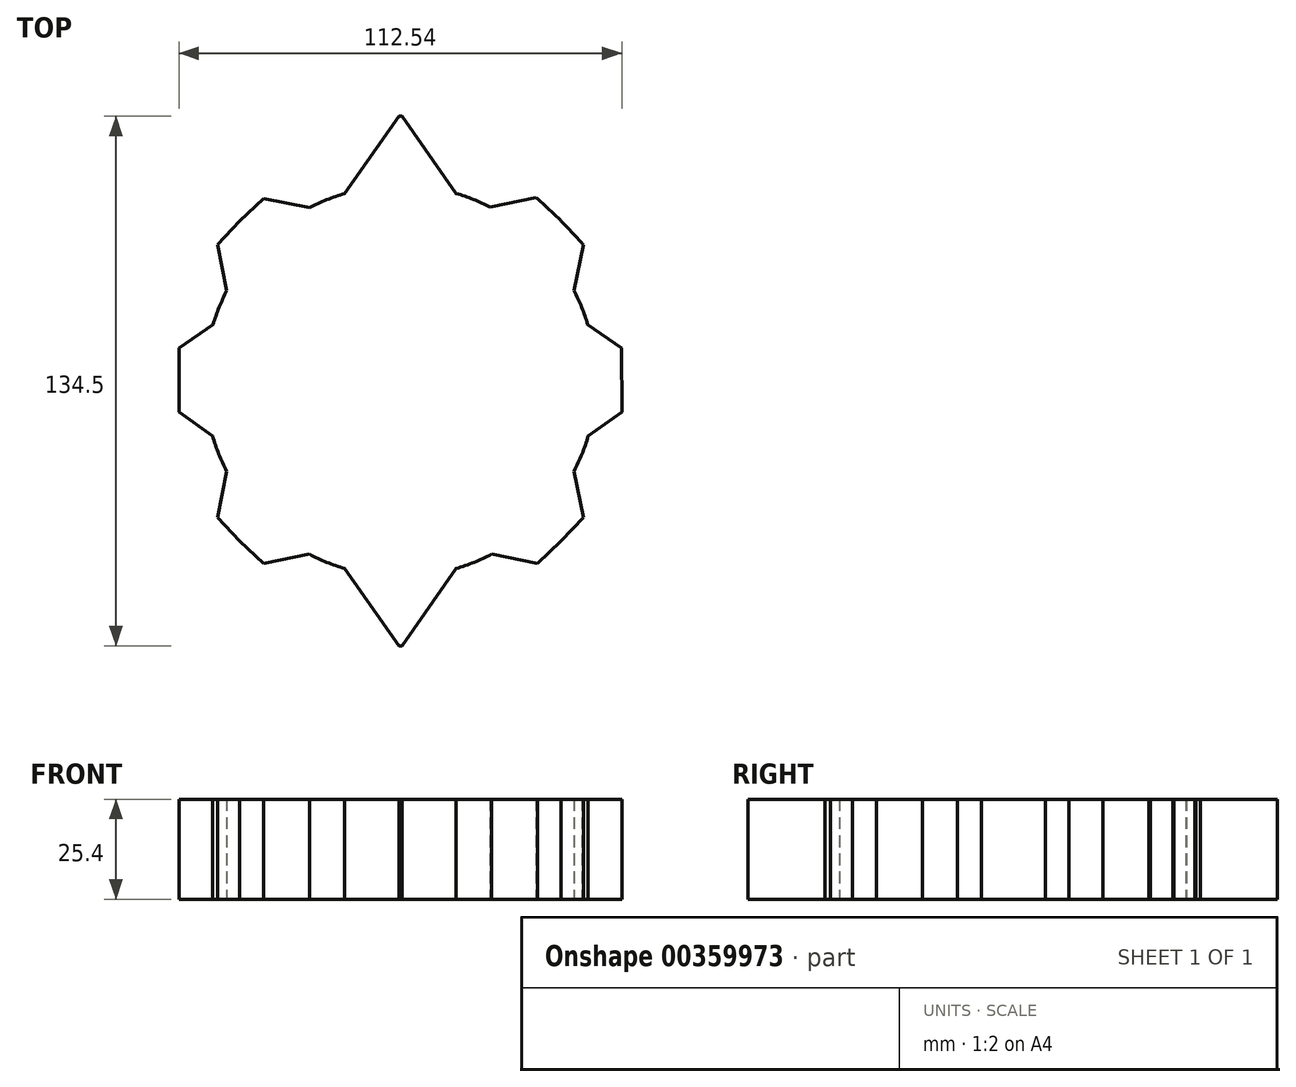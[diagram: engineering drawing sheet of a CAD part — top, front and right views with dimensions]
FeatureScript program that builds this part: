
annotation { "Feature Type Name" : "Feature", "Feature Type Description" : "" }
export const myFeature = defineFeature(function(context is Context, id is Id, definition is map)
    precondition{}
    {
        {
            var Q0;
            Q0=qCreatedBy(makeId("Top.planeOp"),FACE);
            var sketch = newSketch(context, id + "F0", { "sketchPlane" : qUnion([Q0])});
            skCircle(sketch, "E0", {"center": v(0, 0) * mm, "radius": 49.71 * mm});
            skLineSegment(sketch, "E1", {"start": v(0, -67.25) * mm, "end": v(-0.36, -67.25) * mm});
            skLineSegment(sketch, "E2", {"start": v(-0.36, -67.25) * mm, "end": v(-14.16, -47.65) * mm});
            skLineSegment(sketch, "E3.MirrorCS", {"start": v(0.36, -67.25) * mm, "end": v(14.16, -47.65) * mm});
            skLineSegment(sketch, "E4.MirrorCS", {"start": v(0, -67.25) * mm, "end": v(0.36, -67.25) * mm});
            skLineSegment(sketch, "E5.MirrorCS", {"start": v(46.47, -34.62) * mm, "end": v(44.1, -22.94) * mm});
            skLineSegment(sketch, "E6.MirrorCS", {"start": v(40.86, -40.7) * mm, "end": v(46.47, -34.62) * mm});
            skLineSegment(sketch, "E7.MirrorCS", {"start": v(34.82, -46.32) * mm, "end": v(23.13, -44) * mm});
            skLineSegment(sketch, "E8.MirrorCS", {"start": v(40.86, -40.7) * mm, "end": v(34.82, -46.32) * mm});
            skLineSegment(sketch, "E9.MirrorCS", {"start": v(-40.86, -40.7) * mm, "end": v(-34.82, -46.32) * mm});
            skLineSegment(sketch, "E10.MirrorCS", {"start": v(-40.86, -40.7) * mm, "end": v(-46.47, -34.62) * mm});
            skLineSegment(sketch, "E11.MirrorCS", {"start": v(-46.47, -34.62) * mm, "end": v(-44.1, -22.94) * mm});
            skLineSegment(sketch, "E12.MirrorCS", {"start": v(-34.82, -46.32) * mm, "end": v(-23.13, -44) * mm});
            skLineSegment(sketch, "E13.MirrorCS", {"start": v(40.86, 40.7) * mm, "end": v(46.47, 34.62) * mm});
            skLineSegment(sketch, "E14.MirrorCS", {"start": v(40.86, 40.7) * mm, "end": v(34.82, 46.32) * mm});
            skLineSegment(sketch, "E15.MirrorCS", {"start": v(-40.86, 40.7) * mm, "end": v(-46.47, 34.62) * mm});
            skLineSegment(sketch, "E16.MirrorCS", {"start": v(-40.86, 40.7) * mm, "end": v(-34.82, 46.32) * mm});
            skLineSegment(sketch, "E17.MirrorCS", {"start": v(-46.47, 34.62) * mm, "end": v(-44.1, 22.94) * mm});
            skLineSegment(sketch, "E18.MirrorCS", {"start": v(0, 67.25) * mm, "end": v(0.36, 67.25) * mm});
            skLineSegment(sketch, "E19.MirrorCS", {"start": v(-0.36, 67.25) * mm, "end": v(-14.16, 47.65) * mm});
            skLineSegment(sketch, "E20.MirrorCS", {"start": v(-34.82, 46.32) * mm, "end": v(-23.13, 44) * mm});
            skLineSegment(sketch, "E21.MirrorCS", {"start": v(0, 67.25) * mm, "end": v(-0.36, 67.25) * mm});
            skLineSegment(sketch, "E22.MirrorCS", {"start": v(46.47, 34.62) * mm, "end": v(44.1, 22.94) * mm});
            skLineSegment(sketch, "E23.MirrorCS", {"start": v(0.36, 67.25) * mm, "end": v(14.16, 47.65) * mm});
            skLineSegment(sketch, "E24.MirrorCS", {"start": v(34.82, 46.32) * mm, "end": v(23.13, 44) * mm});
            skLineSegment(sketch, "E25.MirrorCS", {"start": v(40.52, 41.03) * mm, "end": v(46.18, 35.02) * mm});
            skLineSegment(sketch, "E26.MirrorCS", {"start": v(40.52, 41.03) * mm, "end": v(34.43, 46.62) * mm});
            skLineSegment(sketch, "E27.MirrorCS", {"start": v(46.18, 35.02) * mm, "end": v(43.9, 23.31) * mm});
            skLineSegment(sketch, "E28.MirrorCS", {"start": v(56.24, 0.24) * mm, "end": v(56.2, 8.35) * mm});
            skLineSegment(sketch, "E29.MirrorCS", {"start": v(34.43, 46.62) * mm, "end": v(22.75, 44.2) * mm});
            skLineSegment(sketch, "E30.MirrorCS", {"start": v(56.27, -7.88) * mm, "end": v(47.71, -13.96) * mm});
            skLineSegment(sketch, "E31.MirrorCS", {"start": v(56.2, 8.35) * mm, "end": v(47.6, 14.36) * mm});
            skLineSegment(sketch, "E32.MirrorCS", {"start": v(56.24, 0.24) * mm, "end": v(56.27, -7.88) * mm});
            skLineSegment(sketch, "E33.MirrorCS", {"start": v(-46.18, 35.02) * mm, "end": v(-43.9, 23.31) * mm});
            skLineSegment(sketch, "E34.MirrorCS", {"start": v(-56.24, 0.24) * mm, "end": v(-56.2, 8.35) * mm});
            skLineSegment(sketch, "E35.MirrorCS", {"start": v(-56.27, -7.88) * mm, "end": v(-47.71, -13.96) * mm});
            skLineSegment(sketch, "E36.MirrorCS", {"start": v(-56.2, 8.35) * mm, "end": v(-47.6, 14.36) * mm});
            skLineSegment(sketch, "E37.MirrorCS", {"start": v(-56.24, 0.24) * mm, "end": v(-56.27, -7.88) * mm});
            skSolve(sketch);
        }
        {
            var Q0;
            Q0 = qSketchRegion(id + "F0", true);
            extrude(context, id + "F1", {"entities" : qUnion([Q0]), "depth" : 25.4 * mm});
        }
    });
